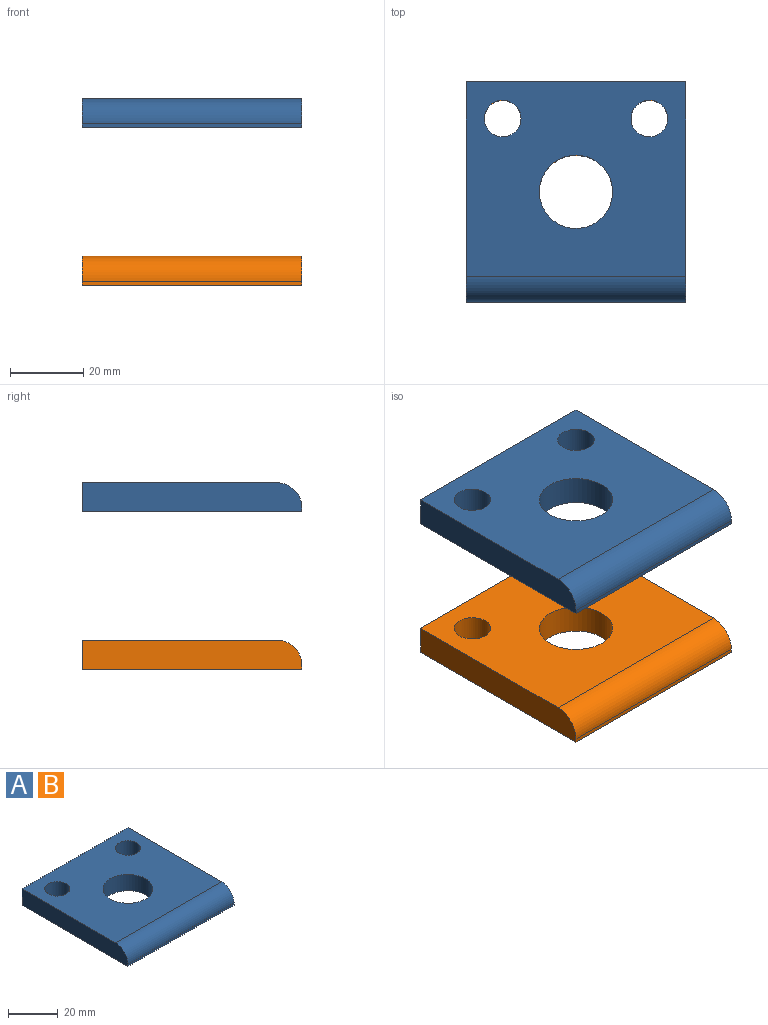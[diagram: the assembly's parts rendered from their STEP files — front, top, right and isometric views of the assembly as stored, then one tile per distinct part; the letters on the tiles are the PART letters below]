
ASSEMBLY  parts=2 mates=3
PART A: 10 faces, bbox 60x60x8 mm
  f0: plane 60x1.08mm, normal (0,-1,0), area 65mm2, adj f1,f6,f8,f9
  f1: plane 60x8mm, normal (1,0,0), area 469.7mm2, adj f0,f2,f7,f8,f9
  f2: plane 60x8mm, normal (0,1,0), area 480mm2, adj f1,f6,f7,f8
  f3: cylinder r=10mm len=20mm, axis (0,0,-1), area 502.7mm2, adj f7,f8
  f4: cylinder r=5mm len=10mm, axis (0,0,-1), area 251.3mm2, adj f7,f8
  f5: cylinder r=5mm len=10mm, axis (0,0,-1), area 251.3mm2, adj f7,f8
  f6: plane 60x8mm, normal (-1,0,0), area 469.7mm2, adj f0,f2,f7,f8,f9
  f7: plane 60x53.08mm, normal (0,0,1), area 2713.8mm2, adj f1,f2,f3,f4,f5,f6,f9
  f8: plane 60x60mm, normal (0,0,-1), area 3128.8mm2, adj f0,f1,f2,f3,f4,f5,f6
  f9: cylinder r=6.92mm len=60mm, axis (-1,0,0), area 651.8mm2, adj f0,f1,f6,f7
PART B: same geometry as A
PLACE A t=(0,0,42.95)mm
PLACE B at identity fixed
MATE cylindrical A.f4 <-> B.f4  axis (0,0,1) through (-20,20,50.95)mm
MATE parallel A.f8 <-> B.f7  axis (0,0,-1) through (-30,0,42.95)mm
MATE cylindrical B.f3 <-> A.f3  axis (0,0,-1) through (0,0,8)mm
